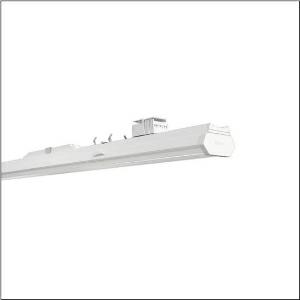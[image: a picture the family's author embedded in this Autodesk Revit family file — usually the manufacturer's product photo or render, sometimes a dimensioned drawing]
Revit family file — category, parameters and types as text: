
# Revit family: licross_r__21_protected_mo_52tp12cn49xg_2097
name_source: partatom
category: Lighting Fixtures
units: mm (PartAtom-declared; Revit-internal decimal feet)

## family parameters
Cut with Voids When Loaded = No
Host = Face
Light Source = No
Part Type = Normal
Room Calculation Point = No
Round Connector Dimension = Use Diameter
Shared = No

## types (1)
- --- (1 x LED, 9110 lm, 50.4 W, 4000K)
    Apparent Load = 50 VA
    CIE Flux Codes = 73 92 98 99 100
    Color Rendering = 80
    Color Temperature = 4000K
    Default Elevation = 1800 mm
    Description = Licross® 21 Protected MO, luminaire insert, of sheet steel, galvanised, coil coated, white, length: 1.500mm, width: 90mm, height: 103mm, LED rated luminous flux: 9.120lm, light colour: 840, control gear: ON/OFF Multilumen, CLOi, control gear: ECG Multilumen, with plug, 3-pole, with phase selection, mains connection: 220..240V, AC, 50/60Hz, start of lifetime: 50W, end of service life: 61W, internal wiring halogen-free, primary light control with lens, of plastic, primary optical cover: cover, of PMMA, light emission: direct distribution, primary light characteristic: symmetric, protection rating (complete): IP64, insulation class (complete): insulation class I (protective earthing), certification: CE, ENEC, VDE, UKCA, protection symbol: D if used in an environment with conductive dust loads with corresponding accessories, impact resistance: IK06, permissible ambient temperature for indoor applications: -35..+45°C, corresponds to IFS (International Featured Standards) requirements for safety and quality in the food industry, reducing of maximum allowable ambient temperature of 5°C with ceiling mounting, LABS conformity tested according to VDMA 24364:2018-05, packaging unit: 1 piece
    Height = 92 mm
    Lamp = 1 x LED
    Lamp Light Flux = 9110 lm
    Lamp Power = 50.4 W
    Lamp count = 1
    Length = 1500 mm
    Luminous efficacy = 181 lm/W
    Manufacturer = Siteco
    ModVariant = No
    Model = 52TP12CN49XG
    Mounting Place = Ceiling
    Mounting Type = Pendant
    Number of Poles = 1
    OnlyDefault = Yes
    Power Factor = 1
    Product Name = Licross® 21 Protected MO
    Product group = luminaire insert | ceiling pendant
    ProductGroupID = 902
    Protection Class = Protection class I
    Protection Degree = IP 64
    RLX_Detail_Level = 1
    RLX_Emergency_Light_Flux = 0 lm
    RLX_Emergency_Type = 0
    RLX_Emergency_Type_DB = No
    RlxData = <blob elided: 22205 chars, md5=0317d6e0>
    Socket = socket
    Standby Power = 0 W
    System Light Flux = 9110 lm
    System Power = 50 W
    Type Comments = factory setting: luminous flux: 100 % | (A | C | E) | 117 mA
    Type Image = l_1256148.jpg
    URL = http://relux.com
    VarID = @adj_132667
    Voltage = 0 V
    Weight = 0.00 kg
    Width = 88 mm

## geometry (parser evidence)
native form markers: Blend x4, Sweep x13
no freeform markers — native parametric forms only
